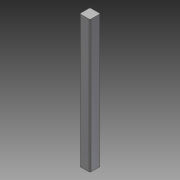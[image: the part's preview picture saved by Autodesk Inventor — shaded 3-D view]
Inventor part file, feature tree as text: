
AUTODESK INVENTOR PART (.ipt)
format: ipt  version: 2014 SP1 (Build 180222100, 222)  size: 77,312 bytes
history: native  units: in
note: dims shown in document units (in); Inventor stores cm internally (conversion verified against a paired STEP export)
features: extrude x1, fillet x1, sketch x1
ambient origin geometry x8: Origin, YZ Plane, XZ Plane, XY Plane, X Axis, Y Axis, Z Axis, Center Point
bodies: Solid1 (feature_tree)
feature tree (3):
  extrude  "Extrusion1"  Depth=0.0787in
  fillet  "Fillet1"  Radius=1.0in
  sketch  "Sketch1"  dims[d0=0.0787in d1=0.0787in d2=1.0in d3=0.0in d4=0.0079in]
